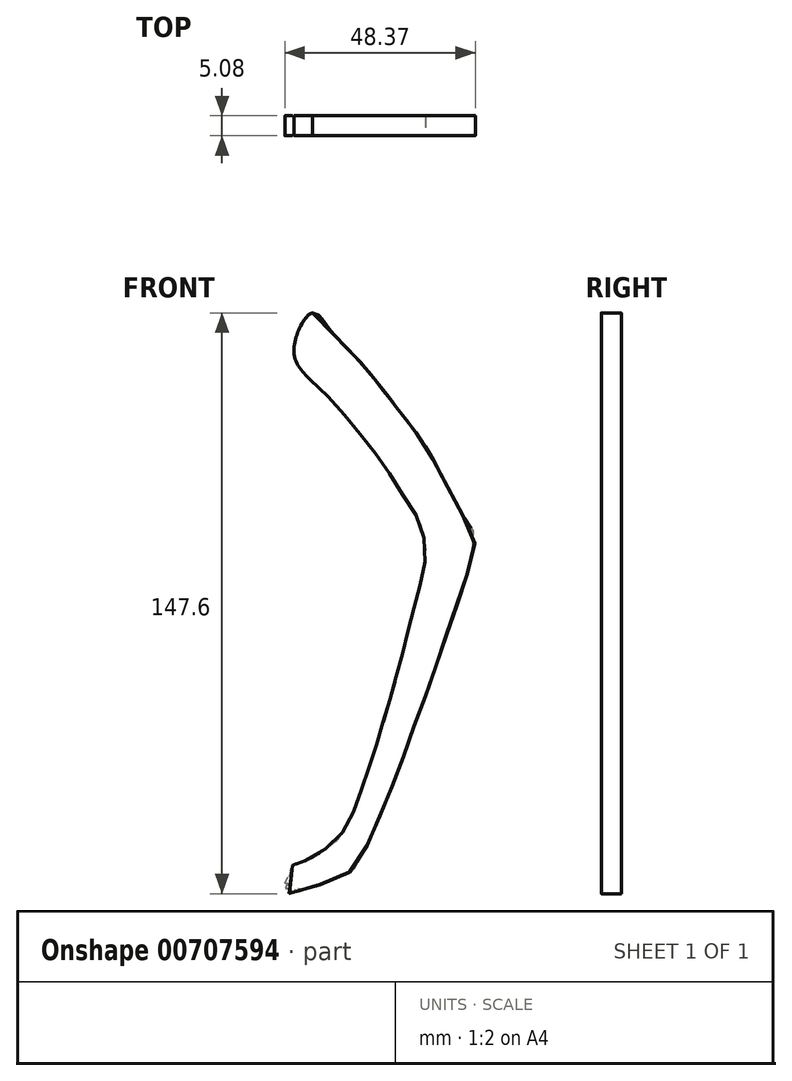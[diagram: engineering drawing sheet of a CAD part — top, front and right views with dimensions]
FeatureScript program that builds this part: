
annotation { "Feature Type Name" : "Feature", "Feature Type Description" : "" }
export const myFeature = defineFeature(function(context is Context, id is Id, definition is map)
    precondition{}
    {
        {
            var Q0;
            Q0=qCreatedBy(makeId("Front.planeOp"),FACE);
            var sketch = newSketch(context, id + "F0", { "sketchPlane" : qUnion([Q0])});
            skLineSegment(sketch, "E0", {"start": v(11.7, 8.56) * mm, "end": v(10.7, -7.18) * mm});
            skLineSegment(sketch, "E1", {"start": v(10.7, -7.18) * mm, "end": v(-10.6, 19) * mm});
            skLineSegment(sketch, "E2", {"start": v(-10.6, 19) * mm, "end": v(-7.8, 82.36) * mm});
            skFitSpline(sketch, "E3", {"points": [v(-7.8, 82.36) * mm, v(-7.24, 98.94) * mm, v(-6.59, 117.12) * mm, v(-5.83, 142.02) * mm, v(-5.45, 168.32) * mm, v(-5.52, 230.34) * mm, v(-6.26, 285.7) * mm, v(-7.2, 315.28) * mm, v(-8.95, 361.43) * mm, v(-10.4, 387.63) * mm, v(-13, 416.84) * mm, v(-15.01, 437.7) * mm, v(-21.29, 480.96) * mm, v(-27.2, 508.68) * mm, v(-28.7, 514.88) * mm], "startDerivative": vector(10.22, 308.11) * mm, "endDerivative": vector(-37.95, 155.7) * mm});
            skLineSegment(sketch, "E4", {"start": v(-28.7, 514.88) * mm, "end": v(-18.5, 504.49) * mm});
            skFitSpline(sketch, "E5", {"points": [v(-18.5, 504.49) * mm, v(-14.2, 494.72) * mm, v(-10.4, 483.17) * mm, v(-6.54, 469.9) * mm, v(-3.1, 457.05) * mm, v(-0.51, 445.6) * mm, v(1.47, 435.93) * mm, v(2.96, 426.2) * mm, v(4.35, 415.6) * mm, v(5.85, 403.15) * mm, v(7.18, 390.92) * mm, v(9.67, 369.53) * mm, v(11.56, 352.56) * mm, v(15.2, 318.42) * mm, v(18.03, 290.8) * mm, v(19.92, 265.34) * mm, v(21.72, 242.6) * mm, v(22.69, 220.79) * mm, v(23.65, 203.25) * mm, v(24.47, 178.85) * mm, v(25.08, 148.77) * mm, v(25.19, 106.94) * mm, v(24.82, 74.57) * mm, v(24.5, 42) * mm], "startDerivative": vector(138.63, -295.52) * mm, "endDerivative": vector(-5.12, -584.15) * mm});
            skFitSpline(sketch, "E6", {"points": [v(24.5, 42) * mm, v(16.7, 39) * mm, v(12.5, 33.24) * mm, v(9.61, 24.95) * mm, v(8.9, 16.91) * mm, v(10.33, 12.23) * mm, v(11.7, 8.56) * mm], "startDerivative": vector(-46.28, -12) * mm, "endDerivative": vector(10.21, -28.51) * mm});
            skFitSpline(sketch, "E7", {"points": [v(-10.6, 84.98) * mm, v(-8.5, 83) * mm, v(-6.65, 78.8) * mm, v(-5.89, 72.07) * mm, v(-5.76, 61.33) * mm, v(-5.64, 47.1) * mm, v(-5.9, 35.6) * mm, v(-6.47, 31.43) * mm, v(-6.34, 26.97) * mm, v(-4.57, 21.8) * mm, v(-2.21, 17.83) * mm, v(0, 15.05) * mm, v(2.28, 13.08) * mm, v(5.76, 11.32) * mm, v(8.69, 10.16) * mm, v(11.04, 8.9) * mm, v(12.38, 7.6) * mm, v(13.09, 5.99) * mm, v(12.89, 2.76) * mm, v(12.15, -3.9) * mm, v(11.7, -8.74) * mm, v(11.08, -13.22) * mm], "startDerivative": vector(59.9, -45.86) * mm, "endDerivative": vector(-14.62, -97.53) * mm});
            skLineSegment(sketch, "E8", {"start": v(11.08, -13.22) * mm, "end": v(11.08, -15.97) * mm});
            skLineSegment(sketch, "E9", {"start": v(11.08, -15.97) * mm, "end": v(-11.03, -15.97) * mm});
            skLineSegment(sketch, "E10", {"start": v(-11.03, -15.97) * mm, "end": v(-11.2, -13.29) * mm});
            skFitSpline(sketch, "E11", {"points": [v(-11.2, -13.29) * mm, v(-11.2, -11.84) * mm, v(-11.2, -5.52) * mm, v(-11.51, 1.49) * mm, v(-12.16, 4.66) * mm, v(-13.4, 9.05) * mm, v(-15.15, 13.55) * mm, v(-16.64, 17.33) * mm, v(-19.12, 23.61) * mm, v(-19.55, 26.56) * mm, v(-18.64, 31.28) * mm, v(-16.79, 35.33) * mm, v(-14.77, 40.57) * mm, v(-13.5, 46.17) * mm, v(-12.6, 53.4) * mm, v(-12.2, 59.96) * mm, v(-12.37, 65.97) * mm, v(-12.16, 73.91) * mm, v(-11.5, 81.04) * mm, v(-11.2, 84.64) * mm, v(-10.6, 84.98) * mm], "startDerivative": vector(-0.12, 43.3) * mm, "endDerivative": vector(35.61, 8.6) * mm});
            skFitSpline(sketch, "E12", {"points": [v(11.08, -13.22) * mm, v(15.57, -17.52) * mm, v(22.06, -24.41) * mm, v(29.6, -33.47) * mm, v(35.84, -41.56) * mm, v(40.17, -47.64) * mm, v(44.57, -55.74) * mm, v(47.94, -62.06) * mm, v(51.06, -67.51) * mm, v(52.42, -69.67) * mm, v(49.81, -81.38) * mm, v(45.5, -94.07) * mm, v(41.24, -106.63) * mm, v(36.2, -120.43) * mm, v(32.84, -130.03) * mm, v(29.35, -138.2) * mm, v(27.78, -142.23) * mm, v(23.27, -152.08) * mm, v(21.3, -154.75) * mm, v(16.02, -157.43) * mm, v(8.58, -160.03) * mm, v(4.77, -160.41) * mm, v(4.83, -154.75) * mm, v(8.26, -152.78) * mm, v(13.03, -150.3) * mm, v(16.97, -147.44) * mm, v(20.66, -141.85) * mm, v(25.37, -129.07) * mm, v(31.66, -108.36) * mm, v(36.51, -89.69) * mm, v(39.56, -77.02) * mm, v(39.75, -72.83) * mm, v(38.74, -67.42) * mm, v(35.21, -61.22) * mm, v(28.26, -50.55) * mm, v(23.02, -43.89) * mm, v(18.43, -38.21) * mm, v(13.22, -32.69) * mm, v(7.93, -27.32) * mm, v(6.6, -20.94) * mm, v(11.08, -13.22) * mm]});
            skLineSegment(sketch, "E13.bottom", {"start": v(-12.44, -13.29) * mm, "end": v(11.54, -13.29) * mm});
            skLineSegment(sketch, "E13.top", {"start": v(-12.44, -29.01) * mm, "end": v(11.54, -29.01) * mm});
            skLineSegment(sketch, "E13.left", {"start": v(-12.44, -13.29) * mm, "end": v(-12.44, -29.01) * mm});
            skLineSegment(sketch, "E13.right", {"start": v(11.54, -13.29) * mm, "end": v(11.54, -29.01) * mm});
            skLineSegment(sketch, "E14", {"start": v(0, -32.56) * mm, "end": v(0, -38.28) * mm});
            skFitSpline(sketch, "E15", {"points": [v(-10.75, -28.03) * mm, v(-9.93, -35.6) * mm, v(-9.25, -45.2) * mm, v(-8.25, -64.06) * mm, v(-7.6, -83.45) * mm, v(-7.55, -95.02) * mm, v(-7.45, -109.5) * mm, v(-7.73, -122.65) * mm, v(-8.29, -138.57) * mm, v(-9.14, -152.56) * mm, v(-9.03, -155.04) * mm], "startDerivative": vector(11.05, -94.6) * mm, "endDerivative": vector(4.37, -43.01) * mm});
            skLineSegment(sketch, "E16", {"start": v(-9.9, -153.6) * mm, "end": v(9.57, -153.6) * mm});
            skFitSpline(sketch, "E17.MirrorCS", {"points": [v(10.75, -28.03) * mm, v(9.93, -35.6) * mm, v(9.25, -45.2) * mm, v(8.25, -64.06) * mm, v(7.6, -83.45) * mm, v(7.55, -95.02) * mm, v(7.45, -109.5) * mm, v(7.73, -122.65) * mm, v(8.29, -138.57) * mm, v(9.14, -152.56) * mm, v(9.03, -155.04) * mm], "startDerivative": vector(-11.05, -94.6) * mm, "endDerivative": vector(-4.37, -43.01) * mm});
            skSolve(sketch);
        }
        {
            var Q0;
            {var subQ4=sQuery(id+"F0.wireOp",EDGE,"E13.right");Q0=makeQuery(id+"F0.imprint","IMPRINT",FACE,{"disambiguationData":[TD([[makeQuery(id+"F0.imprint","IMPRINT",EDGE,{"derivedFrom":subQ4}),1.0]])]});}
            var Q1;
            {var subQ7=sQuery(id+"F0.wireOp",EDGE,"E13.right");Q1=makeQuery(id+"F0.imprint","IMPRINT",FACE,{"disambiguationData":[TD([[makeQuery(id+"F0.imprint","IMPRINT",EDGE,{"derivedFrom":subQ7}),-1.0]])]});}
            var Q2;
            {var subQ0=sQuery(id+"F0.wireOp",EDGE,"E9");var subQ1=sQuery(id+"F0.wireOp",EDGE,"E8");var subQ2=makeQuery(id+"F0.imprint","INTERSECT",VERTEX,{"derivedFrom":[subQ1,subQ0]});Q2=makeQuery(id+"F0.imprint","IMPRINT",FACE,{"disambiguationData":[TD([[makeQuery(id+"F0.imprint","IMPRINT",EDGE,{"disambiguationData":[TD([[subQ2,1.0]])],"derivedFrom":subQ1}),-1.0]])]});}
            var Q3;
            {var subQ0=sQuery(id+"F0.wireOp",EDGE,"E16");var subQ1=sQuery(id+"F0.wireOp",EDGE,"E12");var subQ2=makeQuery(id+"F0.imprint","INTERSECT",VERTEX,{"derivedFrom":[subQ1,subQ0]});Q3=makeQuery(id+"F0.imprint","IMPRINT",FACE,{"disambiguationData":[TD([[makeQuery(id+"F0.imprint","IMPRINT",EDGE,{"disambiguationData":[TD([[subQ2,-1.0]])],"derivedFrom":subQ1}),-1.0]])]});}
            var Q4;
            {var subQ0=sQuery(id+"F0.wireOp",EDGE,"E17.MirrorCS");var subQ1=sQuery(id+"F0.wireOp",EDGE,"E12");var subQ2=makeQuery(id+"F0.imprint","INTERSECT",VERTEX,{"disambiguationData":[OD(1.0)],"derivedFrom":[subQ1,subQ0]});Q4=makeQuery(id+"F0.imprint","IMPRINT",FACE,{"disambiguationData":[TD([[makeQuery(id+"F0.imprint","IMPRINT",EDGE,{"disambiguationData":[TD([[subQ2,-1.0]])],"derivedFrom":subQ1}),-1.0]])]});}
            extrude(context, id + "F1", {"entities" : qUnion([Q0, Q1, Q2, Q3, Q4]), "depth" : 2.54 * mm, "offsetDistance" : 25.4 * mm});
        }
        {
            var Q0;
            Q0=makeQuery(id+"F1.opExtrude","CAP_FACE",FACE,{"disambiguationData":[OSD([sQuery(id+"F0.wireOp",EDGE,"E8"),sQuery(id+"F0.wireOp",EDGE,"E12"),sQuery(id+"F0.wireOp",EDGE,"E13.bottom"),sQuery(id+"F0.wireOp",EDGE,"E13.top"),sQuery(id+"F0.wireOp",EDGE,"E17.MirrorCS")])],"isStart":true});
            extrude(context, id + "F2", {"entities" : qUnion([Q0]), "operationType" : NewBodyOperationType.ADD, "depth" : 2.54 * mm, "offsetDistance" : 25.4 * mm});
        }
        {
            var Q0;
            {var subQ0=sQuery(id+"F0.wireOp",EDGE,"E12");Q0=makeQuery(id+"F2.boolean.opBoolean","MERGE",FACE,{"derivedFrom":[makeQuery(id+"F1.opExtrude","SWEPT_FACE",FACE,{"disambiguationData":[OSD([subQ0])]}),makeQuery(id+"F2.opExtrude","SWEPT_FACE",FACE,{"disambiguationData":[OSD([subQ0])]})]});}
            var Q1;
            Q1=makeQuery(id+"F1.opExtrude","CAP_EDGE",EDGE,{"disambiguationData":[OSD([sQuery(id+"F0.wireOp",EDGE,"E12")])],"isStart":false});
            fillet(context, id + "F3", {"entities" : qUnion([Q0, Q1]), "radius" : 0.05 * mm, "tangentPropagation" : true, "allowEdgeOverflow" : false});
        }
    });
